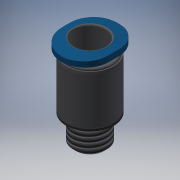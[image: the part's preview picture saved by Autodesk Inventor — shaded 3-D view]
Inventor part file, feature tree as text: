
AUTODESK INVENTOR PART (.ipt)
format: ipt  version: 2017.1 (Build 211199000, 199)  size: 216,064 bytes
history: native  units: mm
features: other x28, sketch x4, revolve x2, extrude x2, thread x1
ambient origin geometry x8: Origin, YZ Plane, XZ Plane, XY Plane, X Axis, Y Axis, Z Axis, Center Point
bodies: Solid1 (feature_tree)
feature tree (37):
  revolve  "Revolution1"  [1 undecoded]
  thread  "Thread1"  [1 undecoded]
  extrude  "Extrusion1"  TaperAngle=360.0deg  [1 undecoded]
  extrude  "Extrusion2"  TaperAngle=0.0deg  [1 undecoded]
  revolve  "Revolution2"  [1 undecoded]
  other  "ANBAU_XY"
  other  "ANBAU_YZ"
  other  "ANBAU_ZX"
  other  "ANBAU_X"
  other  "ANBAU_Y"
  other  "ANBAU_Z"
  other  "ANBAU_Center"
  other  "ANBAU_STD_XY"
  other  "ANBAU_STD_YZ"
  other  "ANBAU_STD_ZX"
  other  "ANBAU_STD_X"
  other  "ANBAU_STD_Y"
  other  "ANBAU_STD_Z"
  other  "ANBAU_STD_Center"
  other  "CPV_XY"
  other  "CPV_YZ"
  other  "CPV_ZX"
  other  "CPV_X"
  other  "CPV_Y"
  other  "CPV_Z"
  other  "CPV_Center"
  other  "CPV_ANBAU_XY"
  other  "CPV_ANBAU_YZ"
  other  "CPV_ANBAU_ZX"
  other  "CPV_ANBAU_X"
  other  "CPV_ANBAU_Y"
  other  "CPV_ANBAU_Z"
  other  "CPV_ANBAU_Center"
  sketch  "Sketch_1"  dims[d0=360.0deg d1=4.3865mm d2=0.0mm d3=1.5mm d4=0.0mm]
  sketch  "Sketch_2"  dims[d5=7.2mm d6=0.0mm d7=360.0deg]
  sketch  "Sketch_3"  dims[d8=0.0mm d9=0.0mm]
  sketch  "Sketch_4"  dims[d10=0.0mm d11=0.0mm]
note: 5 required parameter values undecoded (feature->parameter linkage not recoverable at this tier; creation-order binding heuristic only, values carry confidence <= 0.55)